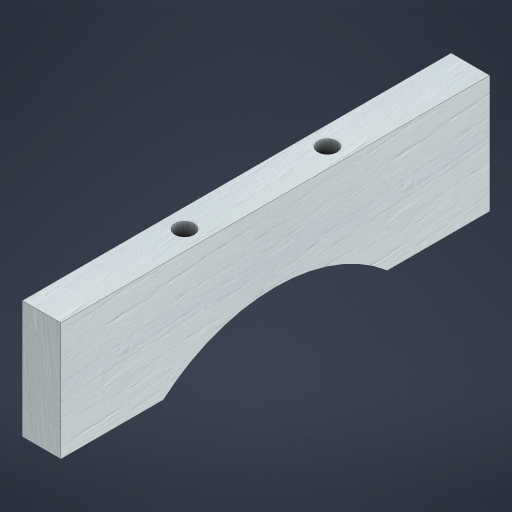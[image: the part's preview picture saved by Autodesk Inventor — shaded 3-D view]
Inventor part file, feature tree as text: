
AUTODESK INVENTOR PART (.ipt)
format: ipt  version: 2024 (Build 280153000, 153)  size: 328,192 bytes
history: native  units: mm
features: extrude x3, other x1, sketch x1
ambient origin geometry x8: Origin, YZ Plane, XZ Plane, XY Plane, X Axis, Y Axis, Z Axis, Center Point
bodies: Body1 (feature_tree)
feature tree (5):
  other  "Sólido1"
  extrude  "Extrusión1"  Depth=18.0mm
  extrude  "Extrusión2"  Depth=18.0mm
  extrude  "Extrusión3"  Depth=18.0mm
  sketch  "Boceto3"  dims[d3=0.0mm d4=9.0mm d5=9.0mm d7=66.666667mm d8=9.0mm d9=9.0mm d10=6.0mm d11=0.0mm d14=100.0mm d15=18.0mm d16=0.0mm]
